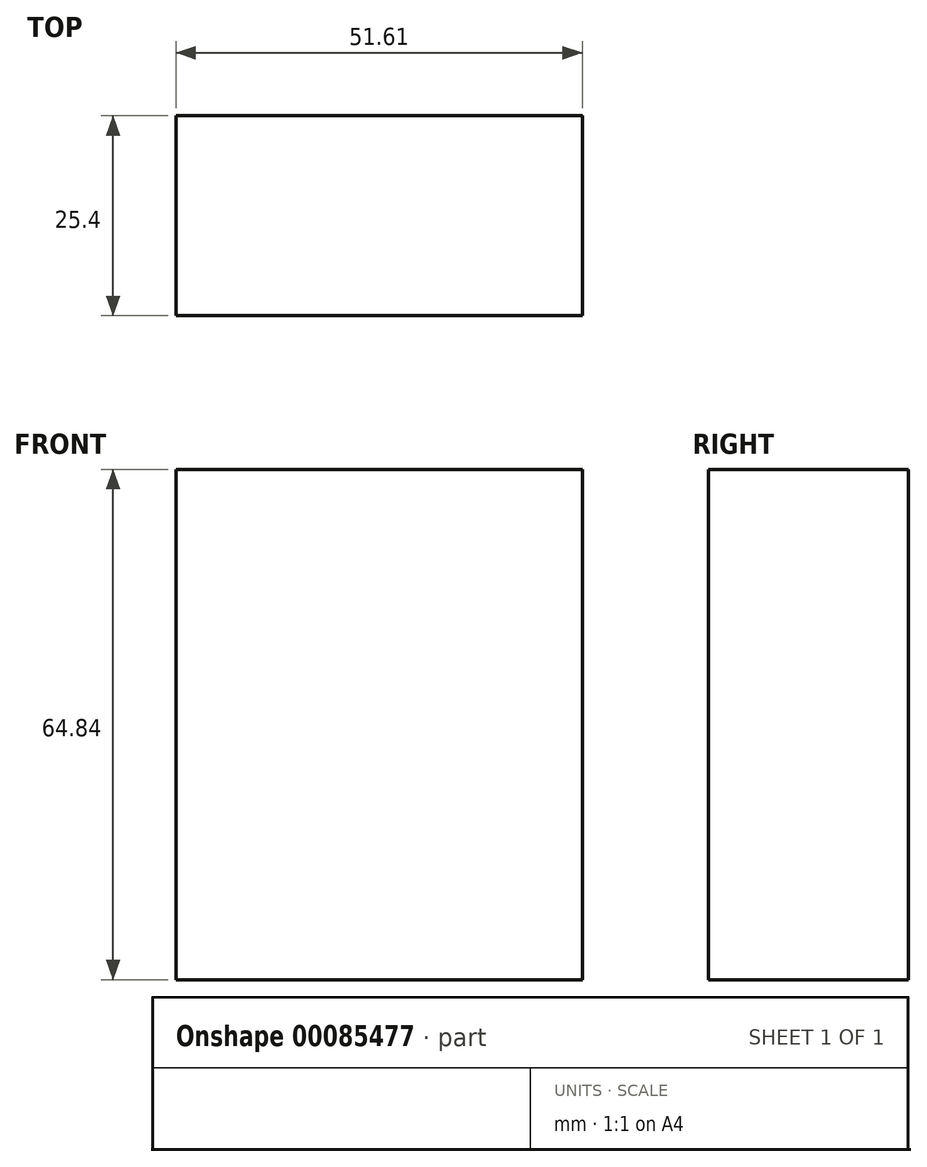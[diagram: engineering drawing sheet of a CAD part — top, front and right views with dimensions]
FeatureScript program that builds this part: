
annotation { "Feature Type Name" : "Feature", "Feature Type Description" : "" }
export const myFeature = defineFeature(function(context is Context, id is Id, definition is map)
    precondition{}
    {
        {
            var Q0;
            Q0=qCreatedBy(makeId("Front.planeOp"),FACE);
            var sketch = newSketch(context, id + "F0", { "sketchPlane" : qUnion([Q0])});
            skLineSegment(sketch, "E0.bottom", {"start": v(-25.68, 5.84) * mm, "end": v(-77.29, 5.84) * mm});
            skLineSegment(sketch, "E0.top", {"start": v(-25.68, -59) * mm, "end": v(-77.29, -59) * mm});
            skLineSegment(sketch, "E0.left", {"start": v(-25.68, 5.84) * mm, "end": v(-25.68, -59) * mm});
            skLineSegment(sketch, "E0.right", {"start": v(-77.29, 5.84) * mm, "end": v(-77.29, -59) * mm});
            skSolve(sketch);
        }
        {
            var Q0;
            Q0=makeQuery(id+"F0.imprint","IMPRINT",FACE,{"disambiguationData":[TD([[makeQuery(id+"F0.imprint","IMPRINT",EDGE,{"derivedFrom":sQuery(id+"F0.wireOp",EDGE,"E0.bottom")}),1.0]])]});
            extrude(context, id + "F1", {"entities" : qUnion([Q0]), "depth" : 25.4 * mm});
        }
    });
